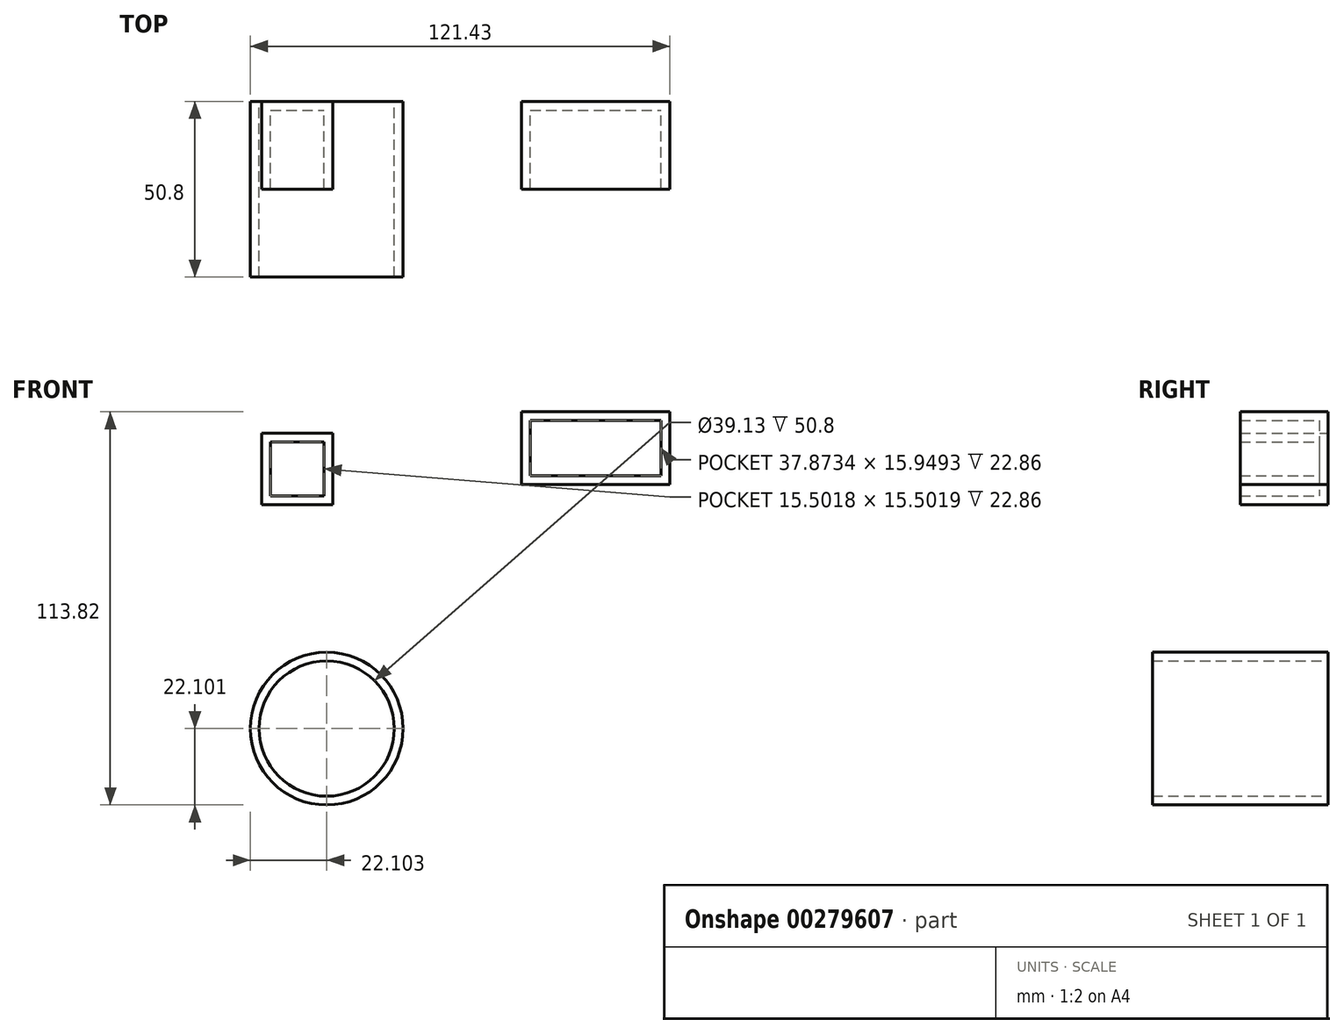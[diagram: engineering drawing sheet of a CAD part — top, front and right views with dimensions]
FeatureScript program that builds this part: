
annotation { "Feature Type Name" : "Feature", "Feature Type Description" : "" }
export const myFeature = defineFeature(function(context is Context, id is Id, definition is map)
    precondition{}
    {
        {
            var Q0;
            Q0=qCreatedBy(makeId("Front.planeOp"),FACE);
            var sketch = newSketch(context, id + "F0", { "sketchPlane" : qUnion([Q0])});
            skLineSegment(sketch, "E0.bottom", {"start": v(-55.93, 45.2) * mm, "end": v(-35.35, 45.2) * mm});
            skLineSegment(sketch, "E0.top", {"start": v(-55.93, 24.6) * mm, "end": v(-35.35, 24.6) * mm});
            skLineSegment(sketch, "E0.left", {"start": v(-55.93, 45.2) * mm, "end": v(-55.93, 24.6) * mm});
            skLineSegment(sketch, "E0.right", {"start": v(-35.35, 45.2) * mm, "end": v(-35.35, 24.6) * mm});
            skLineSegment(sketch, "E1.bottom", {"start": v(9.4, 41.16) * mm, "end": v(51.45, 41.16) * mm});
            skLineSegment(sketch, "E1.top", {"start": v(9.4, 24.6) * mm, "end": v(51.45, 24.6) * mm});
            skLineSegment(sketch, "E1.left", {"start": v(9.4, 41.16) * mm, "end": v(9.4, 24.6) * mm});
            skLineSegment(sketch, "E1.right", {"start": v(51.45, 41.16) * mm, "end": v(51.45, 24.6) * mm});
            skSolve(sketch);
        }
        {
            var Q0;
            Q0=makeQuery(id+"F0.imprint","IMPRINT",FACE,{"disambiguationData":[TD([[makeQuery(id+"F0.imprint","IMPRINT",EDGE,{"derivedFrom":sQuery(id+"F0.wireOp",EDGE,"E0.bottom")}),-1.0]])]});
            extrude(context, id + "F1", {"entities" : qUnion([Q0]), "depth" : 25.4 * mm});
        }
        {
            var Q0;
            Q0=qCreatedBy(makeId("Front.planeOp"),FACE);
            var sketch = newSketch(context, id + "F2", { "sketchPlane" : qUnion([Q0])});
            skLineSegment(sketch, "E2.bottom", {"start": v(19.24, 51.45) * mm, "end": v(62.2, 51.45) * mm});
            skLineSegment(sketch, "E2.top", {"start": v(19.24, 30.43) * mm, "end": v(62.2, 30.43) * mm});
            skLineSegment(sketch, "E2.left", {"start": v(19.24, 51.45) * mm, "end": v(19.24, 30.43) * mm});
            skLineSegment(sketch, "E2.right", {"start": v(62.2, 51.45) * mm, "end": v(62.2, 30.43) * mm});
            skSolve(sketch);
        }
        {
            var Q0;
            Q0=makeQuery(id+"F2.imprint","IMPRINT",FACE,{"disambiguationData":[TD([[makeQuery(id+"F2.imprint","IMPRINT",EDGE,{"derivedFrom":sQuery(id+"F2.wireOp",EDGE,"E2.bottom")}),-1.0]])]});
            extrude(context, id + "F3", {"entities" : qUnion([Q0]), "depth" : 25.4 * mm});
        }
        {
            var Q0;
            Q0=qCreatedBy(makeId("Front.planeOp"),FACE);
            var sketch = newSketch(context, id + "F4", { "sketchPlane" : qUnion([Q0])});
            skCircle(sketch, "E3", {"center": v(-37.14, -40.27) * mm, "radius": 22.1 * mm});
            skSolve(sketch);
        }
        {
            var Q0;
            Q0=makeQuery(id+"F4.imprint","IMPRINT",FACE,{"disambiguationData":[TD([[makeQuery(id+"F4.imprint","IMPRINT",EDGE,{"derivedFrom":sQuery(id+"F4.wireOp",EDGE,"E3")}),1.0]])]});
            extrude(context, id + "F5", {"entities" : qUnion([Q0]), "depth" : 50.8 * mm});
        }
        {
            var Q0;
            Q0=makeQuery(id+"F5.opExtrude","CAP_FACE",FACE,{"disambiguationData":[OSD([sQuery(id+"F4.wireOp",EDGE,"E3")])],"isStart":false});
            var Q1;
            Q1=makeQuery(id+"F5.opExtrude","CAP_FACE",FACE,{"disambiguationData":[OSD([sQuery(id+"F4.wireOp",EDGE,"E3")])],"isStart":true});
            shell(context, id + "F6", {"entities" : qUnion([Q0, Q1]), "thickness" : 2.54 * mm});
        }
        {
            var Q0;
            Q0=makeQuery(id+"F1.opExtrude","CAP_FACE",FACE,{"disambiguationData":[OSD([sQuery(id+"F0.wireOp",EDGE,"E0.bottom"),sQuery(id+"F0.wireOp",EDGE,"E0.top"),sQuery(id+"F0.wireOp",EDGE,"E0.left"),sQuery(id+"F0.wireOp",EDGE,"E0.right")])],"isStart":false});
            shell(context, id + "F7", {"entities" : qUnion([Q0]), "thickness" : 2.54 * mm});
        }
        {
            var Q0;
            Q0=makeQuery(id+"F3.opExtrude","CAP_FACE",FACE,{"disambiguationData":[OSD([sQuery(id+"F2.wireOp",EDGE,"E2.bottom"),sQuery(id+"F2.wireOp",EDGE,"E2.top"),sQuery(id+"F2.wireOp",EDGE,"E2.left"),sQuery(id+"F2.wireOp",EDGE,"E2.right")])],"isStart":false});
            shell(context, id + "F8", {"entities" : qUnion([Q0]), "thickness" : 2.54 * mm});
        }
    });
